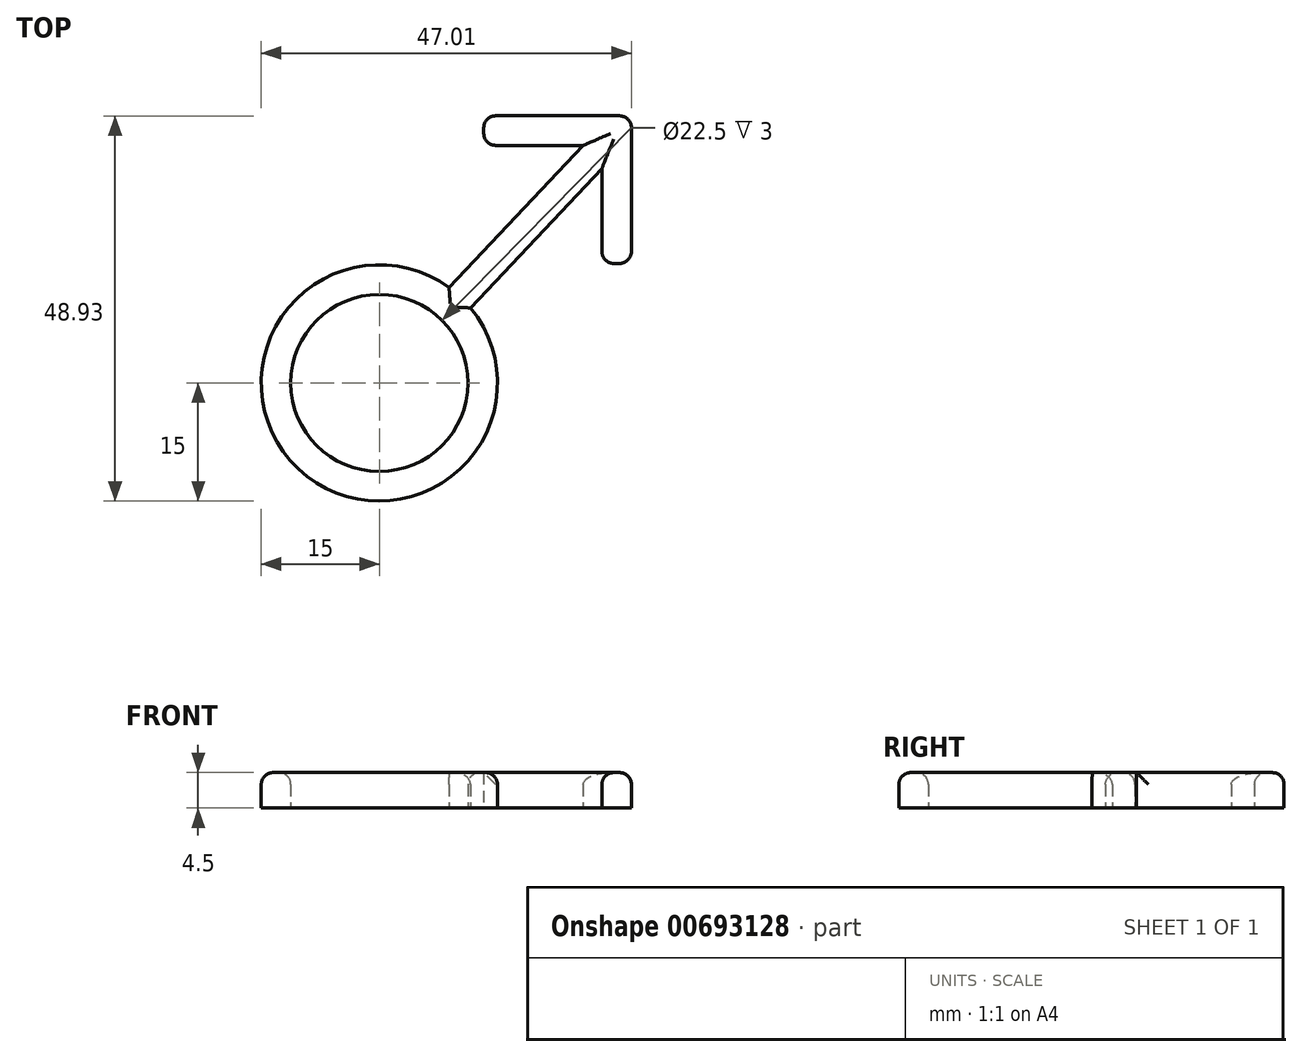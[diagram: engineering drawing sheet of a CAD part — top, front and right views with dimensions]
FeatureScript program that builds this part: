
annotation { "Feature Type Name" : "Feature", "Feature Type Description" : "" }
export const myFeature = defineFeature(function(context is Context, id is Id, definition is map)
    precondition{}
    {
        {
            var Q0;
            Q0=qCreatedBy(makeId("Top.planeOp"),FACE);
            var sketch = newSketch(context, id + "F0", { "sketchPlane" : qUnion([Q0])});
            skPoint(sketch, "E0", {"position": v(0, 0) * mm});
            skCircle(sketch, "E1", {"center": v(0, 0) * mm, "radius": 7.5 * mm});
            skCircle(sketch, "E2", {"center": v(0, 0) * mm, "radius": 10 * mm});
            skLineSegment(sketch, "E3", {"start": v(0, -4.72) * mm, "end": v(0, -33.93) * mm, "construction": true});
            skLineSegment(sketch, "E4", {"start": v(1.25, -29.92) * mm, "end": v(0, -29.92) * mm});
            skLineSegment(sketch, "E5.MirrorCS", {"start": v(-1.25, -29.92) * mm, "end": v(0, -29.92) * mm});
            skLineSegment(sketch, "E6", {"start": v(0, 0) * mm, "end": v(27.29, 28.93) * mm, "construction": true});
            skLineSegment(sketch, "E7", {"start": v(7.72, 6.36) * mm, "end": v(21.44, 20.9) * mm});
            skLineSegment(sketch, "E8", {"start": v(21.44, 20.9) * mm, "end": v(20.53, 21.77) * mm});
            skLineSegment(sketch, "E9.MirrorCS", {"start": v(5.9, 8.07) * mm, "end": v(19.62, 22.62) * mm});
            skLineSegment(sketch, "E10.MirrorCS", {"start": v(19.62, 22.62) * mm, "end": v(20.53, 21.77) * mm});
            skLineSegment(sketch, "E11", {"start": v(21.34, 22.62) * mm, "end": v(8.84, 22.62) * mm});
            skLineSegment(sketch, "E12", {"start": v(21.34, 22.62) * mm, "end": v(21.34, 10.12) * mm});
            skLineSegment(sketch, "E13", {"start": v(21.34, 10.12) * mm, "end": v(18.84, 10.12) * mm});
            skLineSegment(sketch, "E14", {"start": v(8.84, 22.62) * mm, "end": v(8.84, 20.12) * mm});
            skLineSegment(sketch, "E15", {"start": v(8.84, 20.12) * mm, "end": v(17.26, 20.12) * mm});
            skLineSegment(sketch, "E16", {"start": v(18.84, 10.12) * mm, "end": v(18.84, 18.15) * mm});
            skSolve(sketch);
        }
        {
            var Q0;
            Q0=makeQuery(id+"F0.imprint","IMPRINT",FACE,{"disambiguationData":[TD([[makeQuery(id+"F0.imprint","IMPRINT",EDGE,{"derivedFrom":sQuery(id+"F0.wireOp",EDGE,"E1")}),-1.0]])]});
            var Q1;
            {var subQ1=sQuery(id+"F0.wireOp",EDGE,"E2");var subQ5=sQuery(id+"F0.wireOp",EDGE,"L3Ile3Mt-5vU9-O0rP-XFXz-GsDuvshAQ64L");var subQ6=makeQuery(id+"F0.imprint","INTERSECT",VERTEX,{"derivedFrom":[subQ1,subQ5]});Q1=makeQuery(id+"F0.imprint","IMPRINT",FACE,{"disambiguationData":[TD([[makeQuery(id+"F0.imprint","IMPRINT",EDGE,{"disambiguationData":[TD([[subQ6,1.0]])],"derivedFrom":subQ1}),-1.0]])]});}
            var Q2;
            {var subQ5=sQuery(id+"F0.wireOp",EDGE,"yKHzrI7v-d3FW-ei0J-1Jb9-dg8ctSNirIK8");Q2=makeQuery(id+"F0.imprint","IMPRINT",FACE,{"disambiguationData":[TD([[makeQuery(id+"F0.imprint","IMPRINT",EDGE,{"derivedFrom":subQ5}),-1.0]])]});}
            var Q3;
            {var subQ1=sQuery(id+"F0.wireOp",EDGE,"a30OPyKL-WBmp-Hol8-SIYL-npjxL02UYL7A");var subQ3=sQuery(id+"F0.wireOp",EDGE,"L3Ile3Mt-5vU9-O0rP-XFXz-GsDuvshAQ64L");var subQ4=makeQuery(id+"F0.imprint","INTERSECT",VERTEX,{"derivedFrom":[subQ3,subQ1]});Q3=makeQuery(id+"F0.imprint","IMPRINT",FACE,{"disambiguationData":[TD([[makeQuery(id+"F0.imprint","IMPRINT",EDGE,{"disambiguationData":[TD([[subQ4,-1.0]])],"derivedFrom":subQ3}),-1.0]])]});}
            var Q4;
            {var subQ5=sQuery(id+"F0.wireOp",EDGE,"5aefb016-0f08-437b-822c-b709948362630.MirrorCS");Q4=makeQuery(id+"F0.imprint","IMPRINT",FACE,{"disambiguationData":[TD([[makeQuery(id+"F0.imprint","IMPRINT",EDGE,{"derivedFrom":subQ5}),1.0]])]});}
            var Q5;
            {var subQ4=sQuery(id+"F0.wireOp",EDGE,"E4");Q5=makeQuery(id+"F0.imprint","IMPRINT",FACE,{"disambiguationData":[TD([[makeQuery(id+"F0.imprint","IMPRINT",EDGE,{"derivedFrom":subQ4}),-1.0]])]});}
            var Q6;
            {var subQ4=sQuery(id+"F0.wireOp",EDGE,"E14");Q6=makeQuery(id+"F0.imprint","IMPRINT",FACE,{"disambiguationData":[TD([[makeQuery(id+"F0.imprint","IMPRINT",EDGE,{"derivedFrom":subQ4}),1.0]])]});}
            var Q7;
            {var subQ0=sQuery(id+"F0.wireOp",EDGE,"E10.MirrorCS");Q7=makeQuery(id+"F0.imprint","IMPRINT",FACE,{"disambiguationData":[TD([[makeQuery(id+"F0.imprint","IMPRINT",EDGE,{"derivedFrom":subQ0}),1.0]])]});}
            var Q8;
            {var subQ4=sQuery(id+"F0.wireOp",EDGE,"E13");Q8=makeQuery(id+"F0.imprint","IMPRINT",FACE,{"disambiguationData":[TD([[makeQuery(id+"F0.imprint","IMPRINT",EDGE,{"derivedFrom":subQ4}),-1.0]])]});}
            extrude(context, id + "F1", {"entities" : qUnion([Q0, Q1, Q2, Q3, Q4, Q5, Q6, Q7, Q8]), "depth" : 3 * mm, "offsetDistance" : 25 * mm});
        }
        {
            var Q0;
            {var subQ0=sQuery(id+"F0.wireOp",EDGE,"fb005b7b-949a-4557-a6d5-f72ec7387f540.MirrorCS");Q0=makeQuery(id+"F1.opExtrude","CAP_EDGE",EDGE,{"disambiguationData":[OSD([subQ0]),TDD([makeQuery(id+"F0.imprint","IMPRINT",EDGE,{"disambiguationData":[TD([[makeQuery(id+"F0.imprint","INTERSECT",VERTEX,{"derivedFrom":[sQuery(id+"F0.wireOp",EDGE,"E2"),subQ0]}),-1.0]])],"derivedFrom":subQ0})])],"isStart":false});}
            var Q1;
            {var subQ0=sQuery(id+"F0.wireOp",EDGE,"L3Ile3Mt-5vU9-O0rP-XFXz-GsDuvshAQ64L");Q1=makeQuery(id+"F1.opExtrude","CAP_EDGE",EDGE,{"disambiguationData":[OSD([subQ0]),TDD([makeQuery(id+"F0.imprint","IMPRINT",EDGE,{"disambiguationData":[TD([[makeQuery(id+"F0.imprint","INTERSECT",VERTEX,{"derivedFrom":[sQuery(id+"F0.wireOp",EDGE,"E2"),subQ0]}),-1.0]])],"derivedFrom":subQ0})])],"isStart":false});}
            var Q2;
            Q2=makeQuery(id+"F1.opExtrude","CAP_EDGE",EDGE,{"disambiguationData":[OSD([sQuery(id+"F0.wireOp",EDGE,"a30OPyKL-WBmp-Hol8-SIYL-npjxL02UYL7A")])],"isStart":false});
            var Q3;
            Q3=makeQuery(id+"F1.opExtrude","CAP_EDGE",EDGE,{"disambiguationData":[OSD([sQuery(id+"F0.wireOp",EDGE,"m5g99uA3-WRw1-REpf-ayes-NQsWjXoUNYip")])],"isStart":false});
            var Q4;
            Q4=makeQuery(id+"F1.opExtrude","CAP_EDGE",EDGE,{"disambiguationData":[OSD([sQuery(id+"F0.wireOp",EDGE,"46a5b54a-39de-4121-938c-d2ac947e39e10.MirrorCS")])],"isStart":false});
            var Q5;
            Q5=makeQuery(id+"F1.opExtrude","CAP_EDGE",EDGE,{"disambiguationData":[OSD([sQuery(id+"F0.wireOp",EDGE,"2938acd2-b11b-4820-9d41-555befc8a5d10.MirrorCS")])],"isStart":false});
            var Q6;
            {var subQ0=sQuery(id+"F0.wireOp",EDGE,"fb005b7b-949a-4557-a6d5-f72ec7387f540.MirrorCS");Q6=makeQuery(id+"F1.opExtrude","CAP_EDGE",EDGE,{"disambiguationData":[OSD([subQ0]),TDD([makeQuery(id+"F0.imprint","IMPRINT",EDGE,{"disambiguationData":[TD([[makeQuery(id+"F0.imprint","INTERSECT",VERTEX,{"derivedFrom":[subQ0,sQuery(id+"F0.wireOp",EDGE,"E5.MirrorCS")]}),1.0]])],"derivedFrom":subQ0})])],"isStart":false});}
            var Q7;
            {var subQ0=sQuery(id+"F0.wireOp",EDGE,"L3Ile3Mt-5vU9-O0rP-XFXz-GsDuvshAQ64L");Q7=makeQuery(id+"F1.opExtrude","CAP_EDGE",EDGE,{"disambiguationData":[OSD([subQ0]),TDD([makeQuery(id+"F0.imprint","IMPRINT",EDGE,{"disambiguationData":[TD([[makeQuery(id+"F0.imprint","INTERSECT",VERTEX,{"derivedFrom":[subQ0,sQuery(id+"F0.wireOp",EDGE,"E4")]}),1.0]])],"derivedFrom":subQ0})])],"isStart":false});}
            var Q8;
            Q8=makeQuery(id+"F1.opExtrude","CAP_EDGE",EDGE,{"disambiguationData":[OSD([sQuery(id+"F0.wireOp",EDGE,"5aefb016-0f08-437b-822c-b709948362630.MirrorCS")])],"isStart":false});
            var Q9;
            Q9=makeQuery(id+"F1.opExtrude","CAP_EDGE",EDGE,{"disambiguationData":[OSD([sQuery(id+"F0.wireOp",EDGE,"yKHzrI7v-d3FW-ei0J-1Jb9-dg8ctSNirIK8")])],"isStart":false});
            var Q10;
            Q10=makeQuery(id+"F1.opExtrude","CAP_EDGE",EDGE,{"disambiguationData":[OSD([sQuery(id+"F0.wireOp",EDGE,"E2")])],"isStart":false});
            var Q11;
            Q11=makeQuery(id+"F1.opExtrude","CAP_EDGE",EDGE,{"disambiguationData":[OSD([sQuery(id+"F0.wireOp",EDGE,"E1")])],"isStart":false});
            var Q12;
            Q12=makeQuery(id+"F1.opExtrude","CAP_EDGE",EDGE,{"disambiguationData":[OSD([sQuery(id+"F0.wireOp",EDGE,"E4"),sQuery(id+"F0.wireOp",EDGE,"E5.MirrorCS")])],"isStart":false});
            fillet(context, id + "F2", {"entities" : qUnion([Q0, Q1, Q2, Q3, Q4, Q5, Q6, Q7, Q8, Q9, Q10, Q11, Q12]), "radius" : 1 * mm, "tangentPropagation" : true, "allowEdgeOverflow" : false});
        }
        {
            var Q0;
            Q0=makeQuery(id+"F1.opExtrude","CAP_EDGE",EDGE,{"disambiguationData":[OSD([sQuery(id+"F0.wireOp",EDGE,"E7")])],"isStart":false});
            var Q1;
            Q1=makeQuery(id+"F1.opExtrude","CAP_EDGE",EDGE,{"disambiguationData":[OSD([sQuery(id+"F0.wireOp",EDGE,"E9.MirrorCS")])],"isStart":false});
            var Q2;
            Q2=makeQuery(id+"F1.opExtrude","CAP_EDGE",EDGE,{"disambiguationData":[OSD([sQuery(id+"F0.wireOp",EDGE,"E15")])],"isStart":false});
            var Q3;
            Q3=makeQuery(id+"F1.opExtrude","CAP_EDGE",EDGE,{"disambiguationData":[OSD([sQuery(id+"F0.wireOp",EDGE,"E11")])],"isStart":false});
            var Q4;
            Q4=makeQuery(id+"F1.opExtrude","SWEPT_EDGE",EDGE,{"disambiguationData":[OSD([sQuery(id+"F0.wireOp",EDGE,"E11"),sQuery(id+"F0.wireOp",EDGE,"E12")])]});
            var Q5;
            Q5=makeQuery(id+"F1.opExtrude","CAP_EDGE",EDGE,{"disambiguationData":[OSD([sQuery(id+"F0.wireOp",EDGE,"E12")])],"isStart":false});
            var Q6;
            Q6=makeQuery(id+"F1.opExtrude","CAP_EDGE",EDGE,{"disambiguationData":[OSD([sQuery(id+"F0.wireOp",EDGE,"E16")])],"isStart":false});
            var Q7;
            Q7=makeQuery(id+"F1.opExtrude","SWEPT_EDGE",EDGE,{"disambiguationData":[OSD([sQuery(id+"F0.wireOp",EDGE,"E12"),sQuery(id+"F0.wireOp",EDGE,"E13")])]});
            var Q8;
            Q8=makeQuery(id+"F1.opExtrude","SWEPT_EDGE",EDGE,{"disambiguationData":[OSD([sQuery(id+"F0.wireOp",EDGE,"E13"),sQuery(id+"F0.wireOp",EDGE,"E16")])]});
            var Q9;
            Q9=makeQuery(id+"F1.opExtrude","SWEPT_EDGE",EDGE,{"disambiguationData":[OSD([sQuery(id+"F0.wireOp",EDGE,"E14"),sQuery(id+"F0.wireOp",EDGE,"E15")])]});
            var Q10;
            Q10=makeQuery(id+"F1.opExtrude","SWEPT_EDGE",EDGE,{"disambiguationData":[OSD([sQuery(id+"F0.wireOp",EDGE,"E11"),sQuery(id+"F0.wireOp",EDGE,"E14")])]});
            fillet(context, id + "F3", {"entities" : qUnion([Q0, Q1, Q2, Q3, Q4, Q5, Q6, Q7, Q8, Q9, Q10]), "radius" : 1 * mm, "tangentPropagation" : true, "allowEdgeOverflow" : false});
        }
        {
            var Q0;
            Q0=makeQuery(id+"F1.opExtrude","SWEPT_BODY",BODY,{"disambiguationData":[OSD([sQuery(id+"F0.wireOp",EDGE,"E1"),sQuery(id+"F0.wireOp",EDGE,"E2"),sQuery(id+"F0.wireOp",EDGE,"E7"),sQuery(id+"F0.wireOp",EDGE,"E9.MirrorCS"),sQuery(id+"F0.wireOp",EDGE,"E11"),sQuery(id+"F0.wireOp",EDGE,"E12"),sQuery(id+"F0.wireOp",EDGE,"E13"),sQuery(id+"F0.wireOp",EDGE,"E14"),sQuery(id+"F0.wireOp",EDGE,"E15"),sQuery(id+"F0.wireOp",EDGE,"E16")])]});
            var Q1;
            Q1=sQuery(id+"F0.wireOp",VERTEX,"E0");
            transform(context, id + "F4", {"entities" : qUnion([Q0]), "transformType" : TransformType.SCALE_UNIFORMLY, "scale" : 1.5, "scalePoint" : qUnion([Q1]), "makeCopy" : false});
        }
    });
